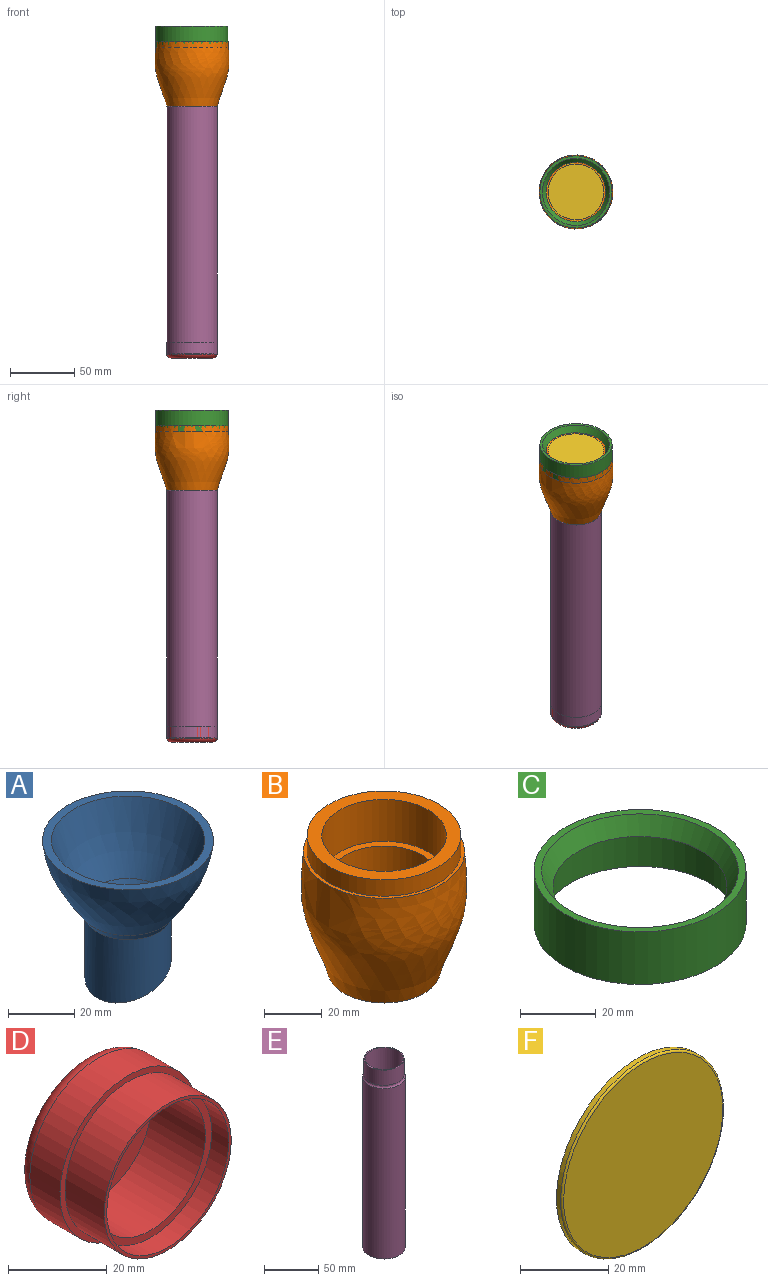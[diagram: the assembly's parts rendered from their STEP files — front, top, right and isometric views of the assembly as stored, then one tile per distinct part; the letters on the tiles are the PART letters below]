
ASSEMBLY  parts=6 mates=6
PART A: 8 faces, bbox 51.7x51.7x52 mm
  f0: cylinder r=10.3mm len=23.49mm, axis (0,0,1), area 1277mm2, adj f2,f7
  f1: cylinder r=13.04mm len=26.08mm, axis (0,0,1), area 1616.7mm2, adj f6,f7
  f2: cone r=10.3mm half-angle=31.2deg, axis (0,0,1), area 364.2mm2, adj f0,f3
  f3: revolved ~46.31x46.31mm, area 2938.9mm2, adj f2,f4
  f4: plane 51.71x51.71mm, normal (0,0,1), area 415.7mm2, adj f3,f5
  f5: revolved ~51.71x51.71mm, area 3704.1mm2, adj f4,f6
  f6: cone r=13.04mm half-angle=31.2deg, axis (0,0,1), area 267mm2, adj f1,f5
  f7: plane 26.08x26.08mm, normal (0.34,0,-0.94), area 213.5mm2, adj f0,f1
PART B: 8 faces, bbox 57.5x57.5x57.4 mm
  f0: plane 55.98x55.98mm, normal (0,0,1), area 222.5mm2, adj f1,f3
  f1: revolved ~57.5x57.5mm, area 8466.1mm2, adj f0,f2
  f2: plane 38.98x38.98mm, normal (0,0,-1), area 81.8mm2, adj f1,f7
  f3: cylinder r=26.7mm len=53.39mm, axis (0,0,-1), area 1165.7mm2, adj f0,f4
  f4: plane 53.39x53.39mm, normal (0,0,1), area 771.7mm2, adj f3,f5
  f5: cylinder r=21.61mm len=43.22mm, axis (0,0,1), area 2416.9mm2, adj f4,f6
  f6: plane 43.22x43.22mm, normal (0,0,1), area 355.6mm2, adj f5,f7
  f7: cylinder r=18.81mm len=39.62mm, axis (0,0,1), area 4682.6mm2, adj f2,f6
PART C: 6 faces, bbox 56x56x17 mm
  f0: plane 56x56mm, normal (0,0,-1), area 339.3mm2, adj f1,f5
  f1: cylinder r=28mm len=56mm, axis (0,0,-1), area 2990.8mm2, adj f0,f2
  f2: plane 56x56mm, normal (0,0,1), area 339.3mm2, adj f1,f3
  f3: cone r=23mm half-angle=30deg, axis (0,0,1), area 923.6mm2, adj f2,f4
  f4: plane 52x52mm, normal (0,0,-1), area 461.8mm2, adj f3,f5
  f5: cylinder r=26mm len=52mm, axis (0,0,-1), area 1928.3mm2, adj f0,f4
PART D: 10 faces, bbox 42.6x23.3x42.6 mm
  f0: cylinder r=19.68mm len=39.35mm, axis (0,1,0), area 1066.9mm2, adj f1,f9
  f1: plane 39.35x39.35mm, normal (0,-1,0), area 177.2mm2, adj f0,f3
  f2: plane 32.35x32.35mm, normal (0,1,0), area 821.9mm2, adj f9
  f3: cylinder r=18.18mm len=36.37mm, axis (0,1,0), area 1279.7mm2, adj f1,f4
  f4: plane 36.37x36.37mm, normal (0,-1,0), area 80.6mm2, adj f3,f5
  f5: cylinder r=17.46mm len=34.93mm, axis (0,-1,0), area 535.5mm2, adj f4,f6
  f6: plane 34.93x34.93mm, normal (0,-1,0), area 187.3mm2, adj f5,f7
  f7: cylinder r=15.66mm len=31.33mm, axis (0,-1,0), area 1521.7mm2, adj f6,f8
  f8: plane 31.33x31.33mm, normal (0,-1,0), area 770.9mm2, adj f7
  f9: torus R=16.17mm, axis (0,-1,0), area 635.7mm2, adj f0,f2
PART E: 6 faces, bbox 39.4x39.4x212 mm
  f0: plane 36.9x36.9mm, normal (0,0,1), area 98.2mm2, adj f4,f5
  f1: plane 39.4x39.4mm, normal (0,0,-1), area 248.3mm2, adj f2,f5
  f2: cylinder r=19.7mm len=192mm, axis (0,0,1), area 23765.5mm2, adj f1,f3
  f3: revolved ~39.4x39.4mm, area 388.8mm2, adj f2,f4
  f4: cylinder r=18.45mm len=36.9mm, axis (0,0,1), area 1988.7mm2, adj f0,f3
  f5: cylinder r=17.58mm len=212mm, axis (0,0,1), area 23417.2mm2, adj f0,f1
PART F: 4 faces, bbox 56.4x1.8x56.4 mm
  f0: cylinder r=26.05mm len=52.1mm, axis (0,1,0), area 214.4mm2, adj f2,f3
  f1: plane 51.1x51.1mm, normal (0,-1,0), area 2050.8mm2, adj f3
  f2: plane 52.1x52.1mm, normal (0,1,0), area 2131.9mm2, adj f0
  f3: torus R=25.55mm, axis (0,-1,0), area 127.7mm2, adj f0,f1
PLACE A t=(59.46,6.25,89.94)mm
PLACE B t=(59.46,6.25,97.19)mm
PLACE C t=(87.46,6.25,92.34)mm
PLACE D rot(axis=(-1,0,0),90deg) t=(59.46,6.25,-148.27)mm
PLACE E t=(59.46,6.25,-82.87)mm
PLACE F rot(axis=(1,0,0),90deg) t=(59.46,6.25,104.14)mm
MATE fastened B.f7 <-> E.f2  axis (0,0,1) through (59.46,6.25,46.72)mm
MATE fastened A.f0 <-> E.f5  axis (0,0,1) through (59.46,6.25,66.72)mm
MATE fastened F.f0 <-> B.f5  axis (0,0,1) through (59.46,6.25,104.14)mm
MATE fastened D.f7 <-> E.f5  axis (0,0,1) through (59.46,6.25,-145.28)mm
MATE fastened C.f1 <-> F.f0  axis (0,0,-1) through (59.46,6.25,104.14)mm
MATE fastened E.f2 <-> B.f7  axis (0,0,1) through (59.46,6.25,46.72)mm
